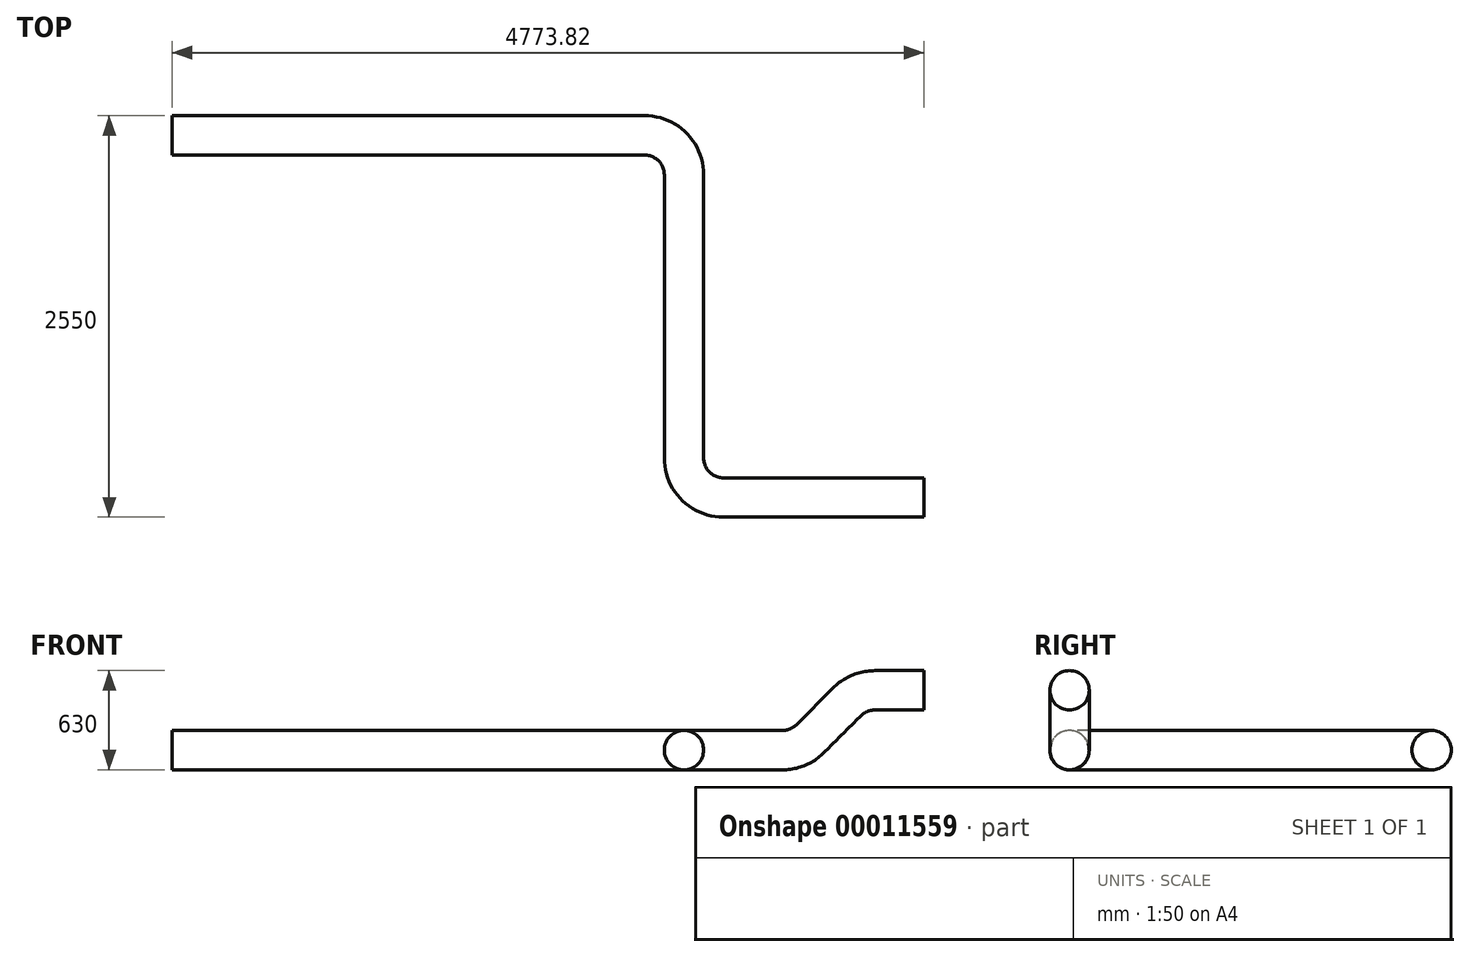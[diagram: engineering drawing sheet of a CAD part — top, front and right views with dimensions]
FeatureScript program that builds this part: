
annotation { "Feature Type Name" : "Feature", "Feature Type Description" : "" }
export const myFeature = defineFeature(function(context is Context, id is Id, definition is map)
    precondition{}
    {
        {
            var Q0;
            Q0=qCreatedBy(makeId("Right.planeOp"),FACE);
            var sketch = newSketch(context, id + "F0", { "sketchPlane" : qUnion([Q0])});
            skCircle(sketch, "E0", {"center": v(0, 0) * mm, "radius": 125 * mm});
            skSolve(sketch);
        }
        {
            var Q0;
            Q0=qCreatedBy(makeId("Front.planeOp"),FACE);
            var sketch = newSketch(context, id + "F1", { "sketchPlane" : qUnion([Q0])});
            skLineSegment(sketch, "E1", {"start": v(0, 0) * mm, "end": v(-311.67, 0) * mm});
            skLineSegment(sketch, "E2", {"start": v(-488.45, -73.22) * mm, "end": v(-722, -306.78) * mm});
            skLineSegment(sketch, "E3", {"start": v(-898.78, -380) * mm, "end": v(-1095.22, -380) * mm});
            skArc(sketch, "E4.filletArc", {"start": v(-311.67, 0) * mm, "mid": v(-407.34, -19.03) * mm, "end": v(-488.45, -73.22) * mm});
            skArc(sketch, "E5.filletArc", {"start": v(-898.78, -380) * mm, "mid": v(-803.1, -360.97) * mm, "end": v(-722, -306.78) * mm});
            skSolve(sketch);
        }
        {
            var Q0;
            Q0 = qSketchRegion(id + "F0", true);
            var Q1;
            Q1 = qBodyType(qCreatedBy(id + "F1" ,EDGE), BodyType.WIRE);
            sweep(context, id + "F2", {"profiles" : qUnion([Q0]), "path" : qUnion([Q1])});
        }
        {
            var Q0;
            Q0=qCreatedBy(makeId("Top.planeOp"),FACE);
            cPlane(context, id + "F3", {"entities" : qUnion([Q0]), "cplaneType" : CPlaneType.OFFSET, "offset" : 380 * mm, "oppositeDirection" : true, "width" : 150 * mm, "height" : 150 * mm});
        }
        {
            var Q0;
            Q0=qCreatedBy(id+"F3.planeOp",FACE);
            var sketch = newSketch(context, id + "F4", { "sketchPlane" : qUnion([Q0])});
            skLineSegment(sketch, "E6", {"start": v(-1095.22, 0) * mm, "end": v(-1273.82, 0) * mm});
            skLineSegment(sketch, "E7", {"start": v(-1523.82, 250) * mm, "end": v(-1523.82, 2050) * mm});
            skLineSegment(sketch, "E8", {"start": v(-1773.82, 2300) * mm, "end": v(-4773.82, 2300) * mm});
            skPoint(sketch, "E9.visualSharp", {"position": v(-1523.82, 2300) * mm});
            skArc(sketch, "E9.filletArc", {"start": v(-1523.82, 2050) * mm, "mid": v(-1597.04, 2226.78) * mm, "end": v(-1773.82, 2300) * mm});
            skPoint(sketch, "E10.visualSharp", {"position": v(-1523.82, 0) * mm});
            skArc(sketch, "E10.filletArc", {"start": v(-1523.82, 250) * mm, "mid": v(-1450.6, 73.22) * mm, "end": v(-1273.82, 0) * mm});
            skSolve(sketch);
        }
        {
            var Q0;
            Q0=makeQuery(id+"F2.opSweep","CAP_FACE",FACE,{"disambiguationData":[OSD([sQuery(id+"F0.wireOp",EDGE,"E0"),sQuery(id+"F1.wireOp",VERTEX,"E3.end")])],"isStart":false});
            var Q1;
            Q1 = qBodyType(qCreatedBy(id + "F4" ,EDGE), BodyType.WIRE);
            sweep(context, id + "F5", {"operationType" : NewBodyOperationType.ADD, "profiles" : qUnion([Q0]), "path" : qUnion([Q1])});
        }
    });
